# Revit family: Apollo 24
name_source: partatom
category: Lighting Fixtures
units: mm (PartAtom-declared; Revit-internal decimal feet)

## family parameters
Cut with Voids When Loaded = No
Host = Face
Light Source = Yes
Part Type = Normal
Room Calculation Point = No
Round Connector Dimension = Use Diameter
Shared = Yes

## types (2) — shared parameters
Apparent Load = 0 VA
AssetType = Fixed installation
Brand = Pholc
Category = Wall lamp
Class = Class 2
Color Filter = 16777215
Default Elevation = 1200 mm
Dimming Lamp Color Temperature Shift = <None>
ElectricalDeviceNominalPower = 20
IFC classification = Light Fixture
IP_Code = IP20
Lamp = LED
Light Source Symbol Length = 200 mm  [stored 0.656168 ft]
LightFixtureMountingType = SURFACE
LightFixturePlacingType = WALL
Lightsource included = No
Lightsource type = Gu10
Manufacturer = Pholc
ManufacturerName = Pholc
ManufacturerURL = https://www.pholc.se
Model = Apollo 24
Name = Apollo 24
Nominal Height = 240 mm  [stored 0.787402 ft]
Nominal Length = 178 mm  [stored 0.58399 ft]
Nominal Width = 126 mm  [stored 0.413386 ft]
NominalCurrent = 0 A
NominalVoltage = 0 V
OmniClass Number = 23-35 47 11
OmniClass Title = Lighting Fixtures
Shape = Cone
Size = 178x126x240
Socket = Gu10
Spot Beam Angle = 80.00°
Spot Field Angle = 80.00°
Tilt Angle = 90.00°
TotalWattage = 20 W
URL = https://www.pholc.se
Uniclass2015Description = Surface luminaires
Uniclass2015Reference = Pr_70_70_48_85
VisualHusRef = Pholc_Id099

## per-type parameters (varying)
| type | ArticleNumber | Color | EAN CODE | Material | Material Outer | ModelNumber | Wattage Comments |
| Apollo 24 - Aluminum | 492224 | Aluminium | 7319684922243 | Aluminium | Aluminum, Anodized Silver | 492224 | 20 |
| Apollo 24 - Darkest hour | 492225 | Black | 7319684922250 | Darkest hour | Aluminum-Black | 492225 | 10 |

note: [stored X ft] marks values corroborated as IEEE doubles in the binary element streams (Revit-internal decimal feet)

## geometry (parser evidence)
native form markers: Sweep x6
no freeform markers — native parametric forms only
